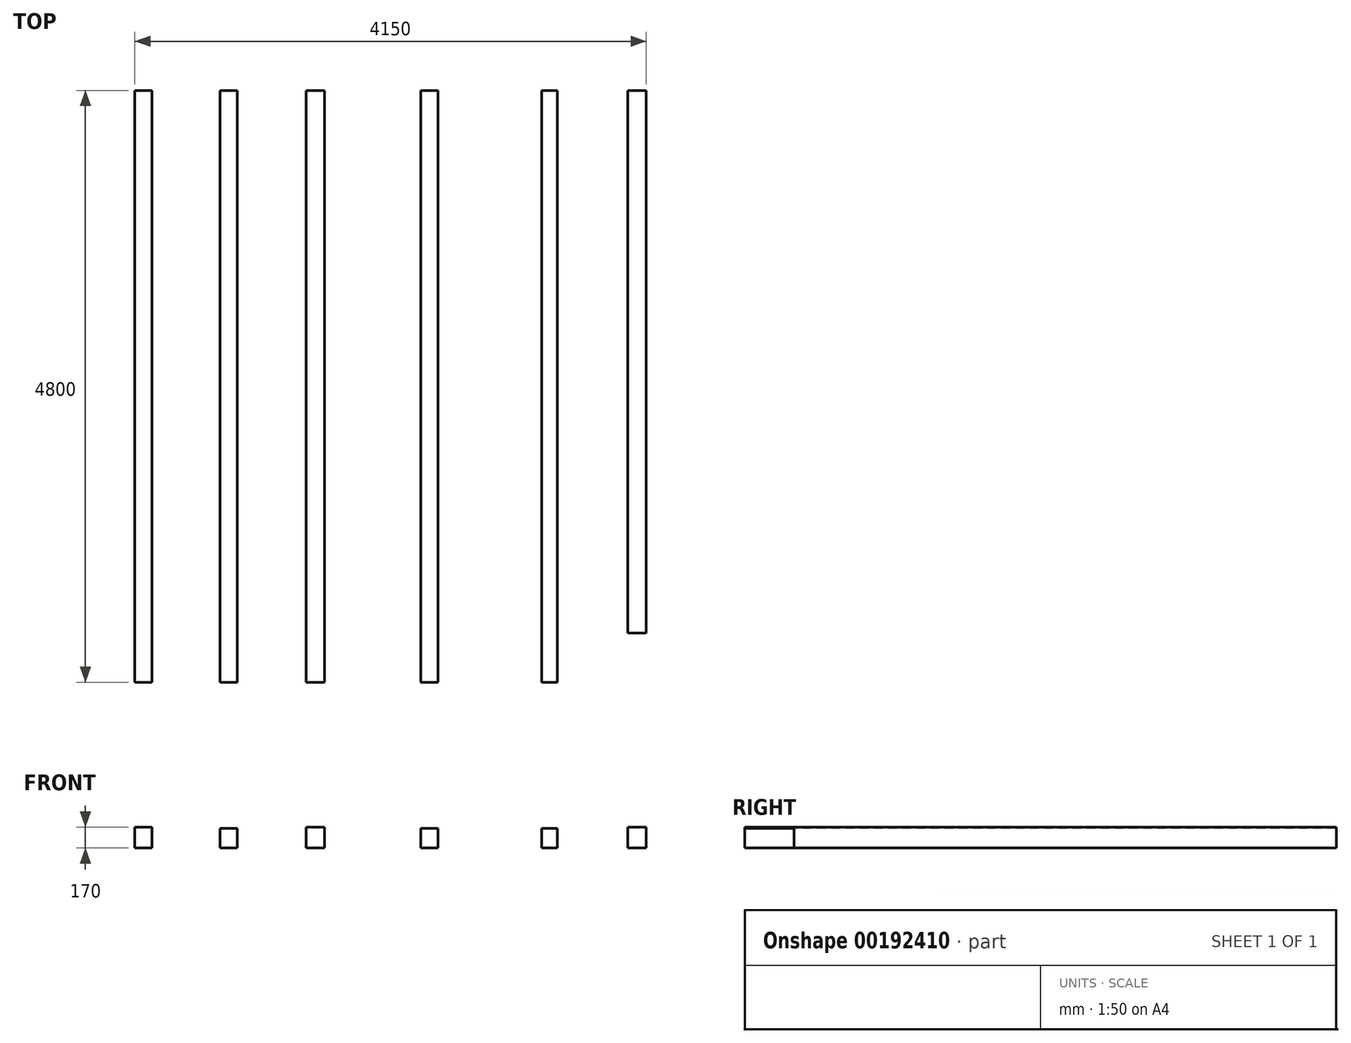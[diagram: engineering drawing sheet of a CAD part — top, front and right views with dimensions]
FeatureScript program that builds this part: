
annotation { "Feature Type Name" : "Feature", "Feature Type Description" : "" }
export const myFeature = defineFeature(function(context is Context, id is Id, definition is map)
    precondition{}
    {
        {
            var Q0;
            Q0=qCreatedBy(makeId("Top.planeOp"),FACE);
            var sketch = newSketch(context, id + "F0", { "sketchPlane" : qUnion([Q0])});
            skLineSegment(sketch, "E0.bottom", {"start": v(-150, 0) * mm, "end": v(0, 0) * mm});
            skLineSegment(sketch, "E1.bottom", {"start": v(-720, 0) * mm, "end": v(-850, 0) * mm});
            skLineSegment(sketch, "E1.top", {"start": v(-720, -4800) * mm, "end": v(-850, -4800) * mm});
            skLineSegment(sketch, "E1.left", {"start": v(-720, 0) * mm, "end": v(-720, -4800) * mm});
            skLineSegment(sketch, "E1.right", {"start": v(-850, 0) * mm, "end": v(-850, -4800) * mm});
            skLineSegment(sketch, "E2.bottom", {"start": v(-1690, 0) * mm, "end": v(-1830, 0) * mm});
            skLineSegment(sketch, "E2.top", {"start": v(-1690, -4800) * mm, "end": v(-1830, -4800) * mm});
            skLineSegment(sketch, "E2.left", {"start": v(-1690, 0) * mm, "end": v(-1690, -4800) * mm});
            skLineSegment(sketch, "E2.right", {"start": v(-1830, 0) * mm, "end": v(-1830, -4800) * mm});
            skLineSegment(sketch, "E3.bottom", {"start": v(-2610, 0) * mm, "end": v(-2760, 0) * mm});
            skLineSegment(sketch, "E3.top", {"start": v(-2610, -4800) * mm, "end": v(-2760, -4800) * mm});
            skLineSegment(sketch, "E3.left", {"start": v(-2610, 0) * mm, "end": v(-2610, -4800) * mm});
            skLineSegment(sketch, "E3.right", {"start": v(-2760, 0) * mm, "end": v(-2760, -4800) * mm});
            skLineSegment(sketch, "E4.bottom", {"start": v(-3320, 0) * mm, "end": v(-3460, 0) * mm});
            skLineSegment(sketch, "E4.top", {"start": v(-3320, -4800) * mm, "end": v(-3460, -4800) * mm});
            skLineSegment(sketch, "E4.left", {"start": v(-3320, 0) * mm, "end": v(-3320, -4800) * mm});
            skLineSegment(sketch, "E4.right", {"start": v(-3460, 0) * mm, "end": v(-3460, -4800) * mm});
            skLineSegment(sketch, "E5.bottom", {"start": v(-4010, 0) * mm, "end": v(-4150, 0) * mm});
            skLineSegment(sketch, "E5.top", {"start": v(-4010, -4800) * mm, "end": v(-4150, -4800) * mm});
            skLineSegment(sketch, "E5.left", {"start": v(-4010, 0) * mm, "end": v(-4010, -4800) * mm});
            skLineSegment(sketch, "E5.right", {"start": v(-4150, 0) * mm, "end": v(-4150, -4800) * mm});
            skPoint(sketch, "E6", {"position": v(0, 0) * mm});
            skLineSegment(sketch, "E7", {"start": v(0, -4400) * mm, "end": v(-720, -4400) * mm});
            skLineSegment(sketch, "E8", {"start": v(-720, -4400) * mm, "end": v(-720, -4550) * mm});
            skLineSegment(sketch, "E9", {"start": v(-720, -4550) * mm, "end": v(500, -4550) * mm});
            skLineSegment(sketch, "E10", {"start": v(500, -4550) * mm, "end": v(500, -4400) * mm});
            skLineSegment(sketch, "E11", {"start": v(500, -4400) * mm, "end": v(0, -4400) * mm});
            skLineSegment(sketch, "E12", {"start": v(-150, 0) * mm, "end": v(-150, -4400) * mm});
            skLineSegment(sketch, "E13", {"start": v(0, 0) * mm, "end": v(0, -4400) * mm});
            skSolve(sketch);
        }
        {
            var Q0;
            Q0=makeQuery(id+"F0.imprint","IMPRINT",FACE,{"disambiguationData":[TD([[makeQuery(id+"F0.imprint","IMPRINT",EDGE,{"derivedFrom":sQuery(id+"F0.wireOp",EDGE,"E5.bottom")}),1.0]])]});
            var Q1;
            Q1=makeQuery(id+"F0.imprint","IMPRINT",FACE,{"disambiguationData":[TD([[makeQuery(id+"F0.imprint","IMPRINT",EDGE,{"derivedFrom":sQuery(id+"F0.wireOp",EDGE,"E3.bottom")}),1.0]])]});
            var Q2;
            Q2=makeQuery(id+"F0.imprint","IMPRINT",FACE,{"disambiguationData":[TD([[makeQuery(id+"F0.imprint","IMPRINT",EDGE,{"derivedFrom":sQuery(id+"F0.wireOp",EDGE,"E0.bottom")}),-1.0]])]});
            extrude(context, id + "F1", {"entities" : qUnion([Q0, Q1, Q2]), "depth" : 170 * mm});
        }
        {
            var Q0;
            Q0=makeQuery(id+"F0.imprint","IMPRINT",FACE,{"disambiguationData":[TD([[makeQuery(id+"F0.imprint","IMPRINT",EDGE,{"derivedFrom":sQuery(id+"F0.wireOp",EDGE,"E4.bottom")}),1.0]])]});
            var Q1;
            Q1=makeQuery(id+"F0.imprint","IMPRINT",FACE,{"disambiguationData":[TD([[makeQuery(id+"F0.imprint","IMPRINT",EDGE,{"derivedFrom":sQuery(id+"F0.wireOp",EDGE,"E2.bottom")}),1.0]])]});
            var Q2;
            Q2=makeQuery(id+"F0.imprint","IMPRINT",FACE,{"disambiguationData":[TD([[makeQuery(id+"F0.imprint","IMPRINT",EDGE,{"derivedFrom":sQuery(id+"F0.wireOp",EDGE,"E1.bottom")}),1.0]])]});
            var Q3;
            {var subQ0=sQuery(id+"F0.wireOp",EDGE,"E8");Q3=makeQuery(id+"F0.imprint","IMPRINT",FACE,{"disambiguationData":[TD([[makeQuery(id+"F0.imprint","IMPRINT",EDGE,{"derivedFrom":subQ0}),1.0]])]});}
            extrude(context, id + "F2", {"entities" : qUnion([Q0, Q1, Q2, Q3]), "depth" : 160 * mm});
        }
    });
